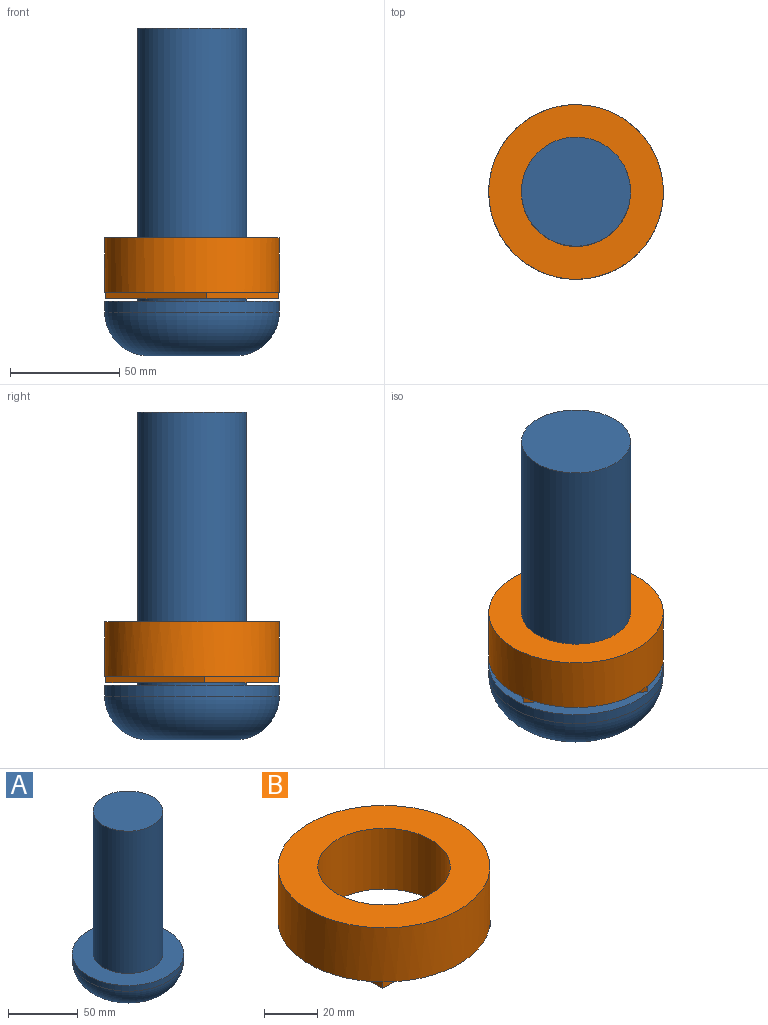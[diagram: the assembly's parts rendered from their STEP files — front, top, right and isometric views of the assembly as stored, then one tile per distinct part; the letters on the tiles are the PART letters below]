
ASSEMBLY  parts=2 mates=1
PART A: 6 faces, bbox 86.6x86.6x150 mm
  f0: cylinder r=25mm len=125mm, axis (0,0,-1), area 19635mm2, adj f1,f3
  f1: plane 50x50mm, normal (0,0,1), area 1963.5mm2, adj f0
  f2: cylinder r=40mm len=80mm, axis (0,0,-1), area 1256.6mm2, adj f3,f5
  f3: plane 80x80mm, normal (0,0,1), area 3063.1mm2, adj f0,f2
  f4: plane 40x40mm, normal (0,0,-1), area 1256.6mm2, adj f5
  f5: torus R=20mm, axis (0,0,1), area 6461.1mm2, adj f2,f4
PART B: 12 faces, bbox 80x80x28 mm
  f0: plane 57.13x12mm, normal (0,0,-1), area 472.8mm2, adj f3,f7
  f1: plane 56x11.43mm, normal (0,0,-1), area 440.8mm2, adj f3,f8
  f2: plane 57.13x12mm, normal (0,0,-1), area 472.8mm2, adj f3,f9
  f3: cylinder r=40mm len=80mm, axis (0,0,-1), area 6283.2mm2, adj f0,f1,f2,f5,f6
  f4: cylinder r=25mm len=50mm, axis (0,0,-1), area 4398.2mm2, adj f5,f11
  f5: plane 80x80mm, normal (0,0,1), area 3063.1mm2, adj f3,f4
  f6: plane 56x11.43mm, normal (0,0,-1), area 440.8mm2, adj f3,f10
  f7: plane 57.13x3mm, normal (0,-1,0), area 171.4mm2, adj f0,f8,f10,f11
  f8: plane 56x3mm, normal (1,0,0), area 168mm2, adj f1,f7,f9,f11
  f9: plane 57.13x3mm, normal (0,1,0), area 171.4mm2, adj f2,f8,f10,f11
  f10: plane 56x3mm, normal (-1,0,0), area 168mm2, adj f6,f7,f9,f11
  f11: plane 57.13x56mm, normal (0,0,-1), area 1235.9mm2, adj f4,f7,f8,f9,f10
PLACE A rot(axis=(0,0,-1),72deg) t=(40.55,84.98,-53.02)mm
PLACE B rot(axis=(0,0,1),144deg) t=(40.55,84.98,-24.02)mm
MATE cylindrical A.f0 <-> B.f3  axis (0,0,-1) through (40.55,84.98,-28.02)mm
